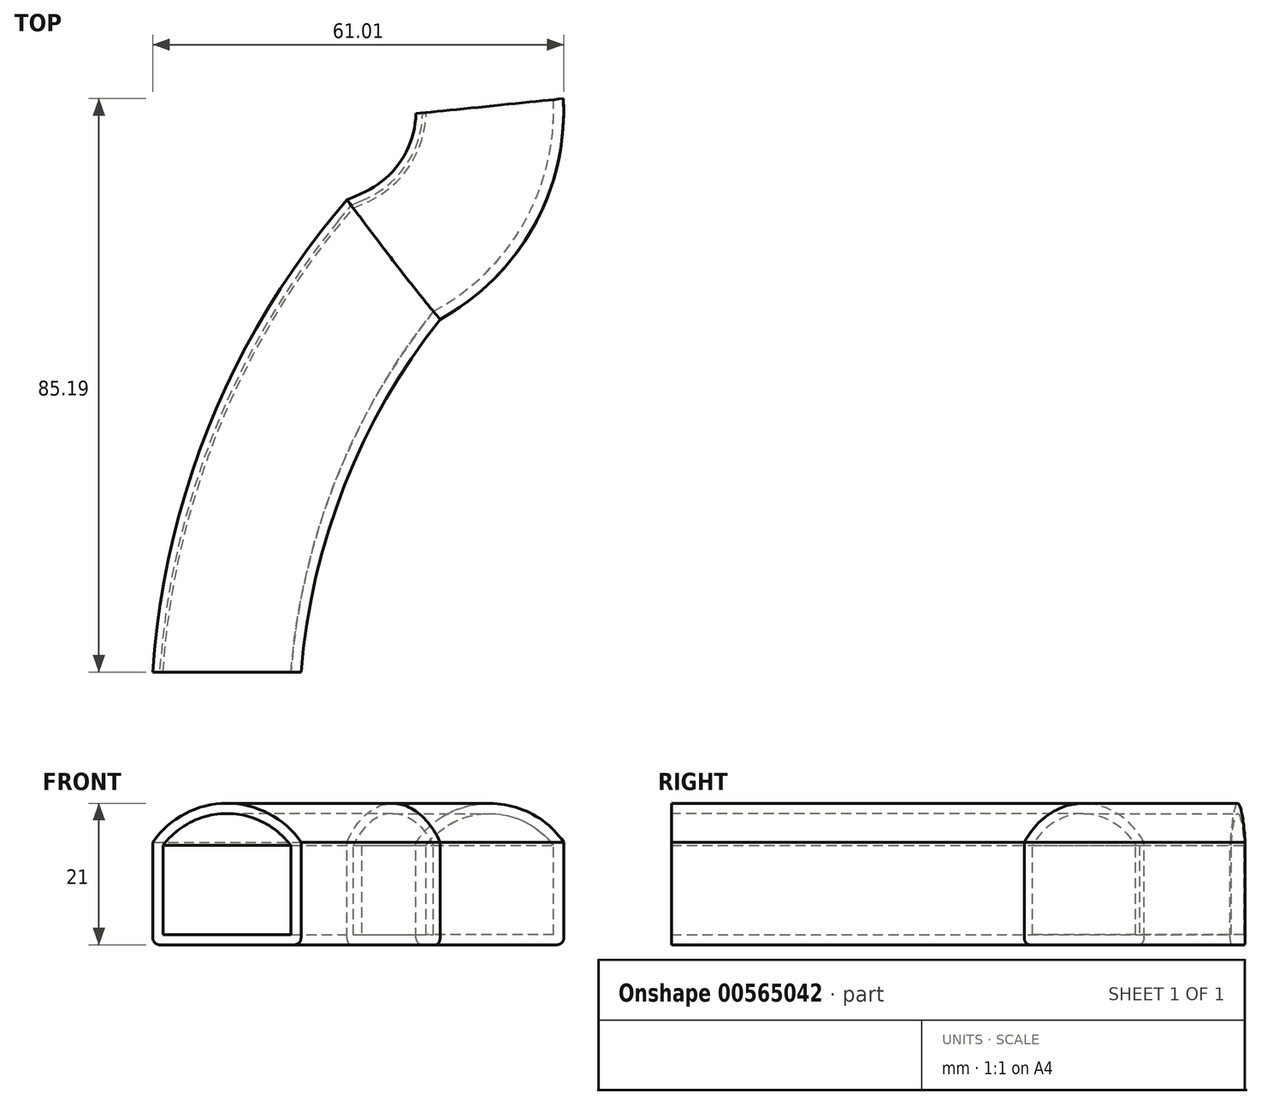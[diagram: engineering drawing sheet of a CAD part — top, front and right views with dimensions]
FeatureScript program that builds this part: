
annotation { "Feature Type Name" : "Feature", "Feature Type Description" : "" }
export const myFeature = defineFeature(function(context is Context, id is Id, definition is map)
    precondition{}
    {
        {
            var Q0;
            Q0=qCreatedBy(makeId("Front.planeOp"),FACE);
            var sketch = newSketch(context, id + "F0", { "sketchPlane" : qUnion([Q0])});
            skLineSegment(sketch, "E0", {"start": v(-1, 0) * mm, "end": v(-21, 0) * mm});
            skArc(sketch, "E1", {"start": v(0, 15.24) * mm, "mid": v(-11, 21) * mm, "end": v(-22, 15.24) * mm});
            skLineSegment(sketch, "E2", {"start": v(-22, 1) * mm, "end": v(-22, 15.24) * mm});
            skLineSegment(sketch, "E3", {"start": v(0, 1) * mm, "end": v(0, 15.24) * mm});
            skPoint(sketch, "E4.visualSharp", {"position": v(-22, 0) * mm});
            skArc(sketch, "E4.filletArc", {"start": v(-22, 1) * mm, "mid": v(-21.7, 0.3) * mm, "end": v(-21, 0) * mm});
            skPoint(sketch, "E5.visualSharp", {"position": v(0, 0) * mm});
            skArc(sketch, "E5.filletArc", {"start": v(-1, 0) * mm, "mid": v(-0.3, 0.3) * mm, "end": v(0, 1) * mm});
            skSolve(sketch);
        }
        {
            var Q0;
            Q0=qCreatedBy(makeId("Top.planeOp"),FACE);
            var sketch = newSketch(context, id + "F1", { "sketchPlane" : qUnion([Q0])});
            skArc(sketch, "E6", {"start": v(13.5, 61.34) * mm, "mid": v(-3.63, 32.6) * mm, "end": v(-11.2, 0) * mm});
            skArc(sketch, "E7", {"start": v(13.5, 61.34) * mm, "mid": v(24.11, 70.52) * mm, "end": v(27.82, 84.05) * mm});
            skSolve(sketch);
        }
        {
            var Q0;
            Q0=makeQuery(id+"F0.imprint","IMPRINT",FACE,{"disambiguationData":[TD([[makeQuery(id+"F0.imprint","IMPRINT",EDGE,{"derivedFrom":sQuery(id+"F0.wireOp",EDGE,"E0")}),-1.0]])]});
            var Q1;
            Q1=sQuery(id+"F1.wireOp",EDGE,"E6");
            var Q2;
            Q2=sQuery(id+"F1.wireOp",EDGE,"E7");
            sweep(context, id + "F2", {"profiles" : qUnion([Q0]), "path" : qUnion([Q1, Q2])});
        }
        {
            var Q0;
            Q0=makeQuery(id+"F2.opSweep","CAP_FACE",FACE,{"disambiguationData":[OSD([sQuery(id+"F0.wireOp",EDGE,"E0"),sQuery(id+"F0.wireOp",EDGE,"E1"),sQuery(id+"F0.wireOp",EDGE,"E2"),sQuery(id+"F0.wireOp",EDGE,"E3"),sQuery(id+"F0.wireOp",EDGE,"E4.filletArc"),sQuery(id+"F0.wireOp",EDGE,"E5.filletArc"),sQuery(id+"F1.wireOp",VERTEX,"E6.end")])],"isStart":true});
            var Q1;
            Q1=makeQuery(id+"F2.opSweep","CAP_FACE",FACE,{"disambiguationData":[OSD([sQuery(id+"F0.wireOp",EDGE,"E0"),sQuery(id+"F0.wireOp",EDGE,"E1"),sQuery(id+"F0.wireOp",EDGE,"E2"),sQuery(id+"F0.wireOp",EDGE,"E3"),sQuery(id+"F0.wireOp",EDGE,"E4.filletArc"),sQuery(id+"F0.wireOp",EDGE,"E5.filletArc"),sQuery(id+"F1.wireOp",VERTEX,"E7.end")])],"isStart":false});
            shell(context, id + "F3", {"entities" : qUnion([Q0, Q1]), "thickness" : 1.5 * mm});
        }
    });
